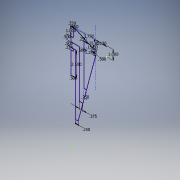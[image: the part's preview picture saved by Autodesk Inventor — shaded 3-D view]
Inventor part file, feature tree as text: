
AUTODESK INVENTOR PART (.ipt)
format: ipt  version: 2017 (Build 210142000, 142)  size: 115,200 bytes
history: native  units: in
note: dims shown in document units (in); Inventor stores cm internally (conversion verified against a paired STEP export)
features: sketch x1
ambient origin geometry x8: Origin, YZ Plane, XZ Plane, XY Plane, X Axis, Y Axis, Z Axis, Center Point
feature tree (1):
  sketch  "Sketch1"  dims[d0=1.13in d1=3.75in d2=0.25in d3=0.1718in d5=1.0in d6=1.0in d7=90.0deg d8=0.5in d9=15.0deg d11=0.25in d12=1.25in d13=0.25in d15=0.25in d16=0.5in d17=0.5in d18=0.5in d19=2.5in d20=0.5in d22=0.375in d23=0.25in d25=0.234in d26=15.0deg]
